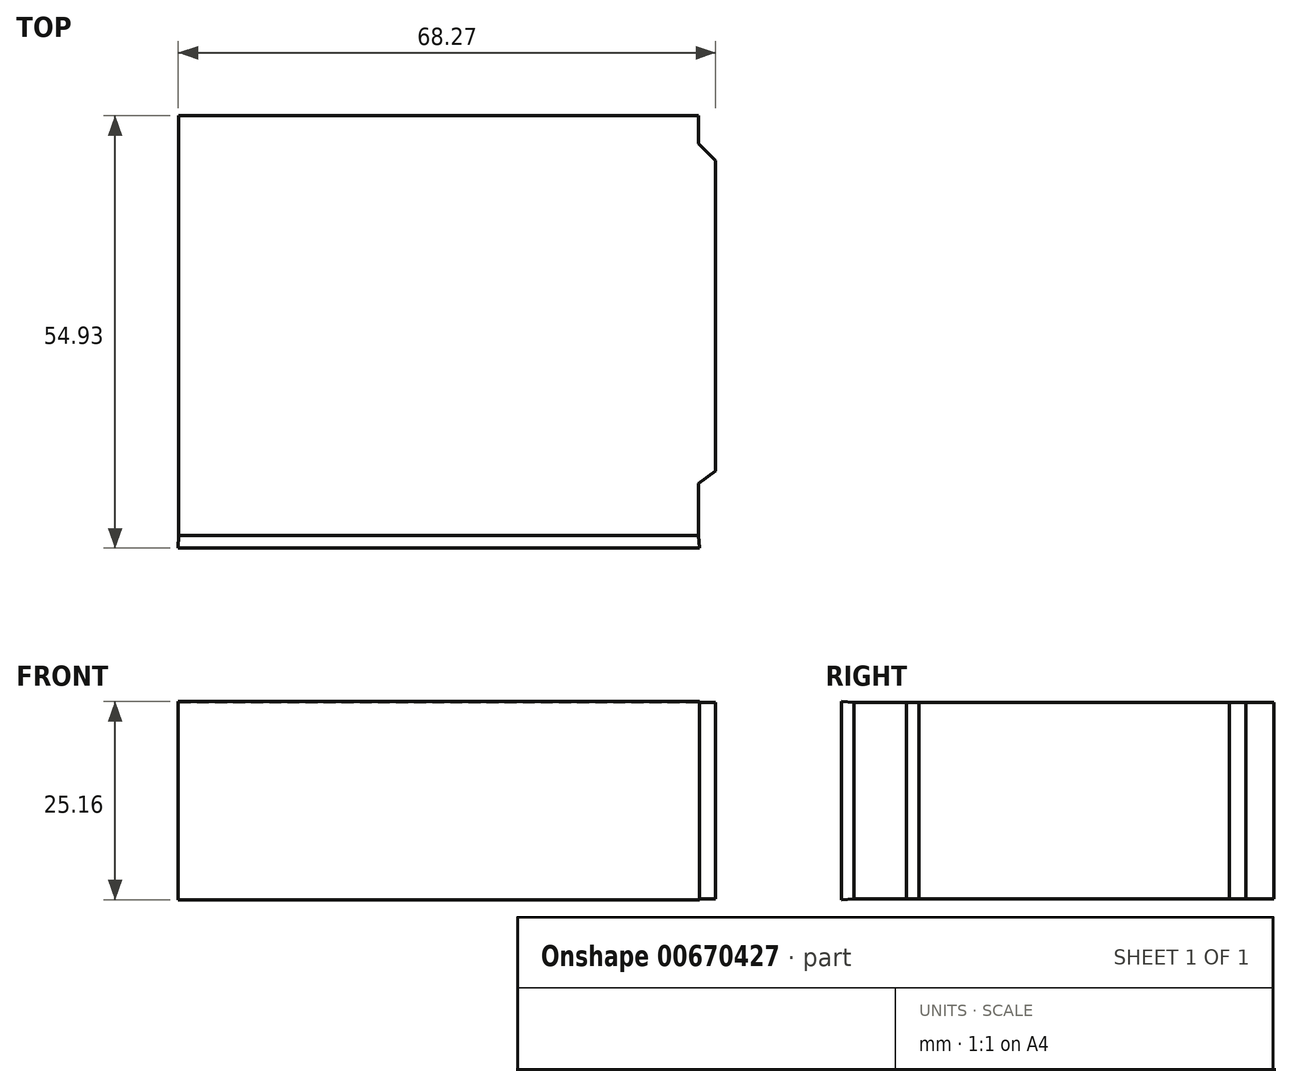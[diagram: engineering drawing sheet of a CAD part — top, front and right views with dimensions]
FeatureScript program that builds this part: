
annotation { "Feature Type Name" : "Feature", "Feature Type Description" : "" }
export const myFeature = defineFeature(function(context is Context, id is Id, definition is map)
    precondition{}
    {
        {
            var Q0;
            Q0=qCreatedBy(makeId("Top.planeOp"),FACE);
            var sketch = newSketch(context, id + "F0", { "sketchPlane" : qUnion([Q0])});
            skLineSegment(sketch, "E0", {"start": v(-33.63, 23.99) * mm, "end": v(32.41, 23.99) * mm});
            skLineSegment(sketch, "E1", {"start": v(32.41, 23.99) * mm, "end": v(32.41, 20.43) * mm});
            skLineSegment(sketch, "E2", {"start": v(-33.63, -29.35) * mm, "end": v(-33.63, 23.99) * mm});
            skLineSegment(sketch, "E3", {"start": v(34.56, 18.29) * mm, "end": v(34.56, -21.13) * mm});
            skLineSegment(sketch, "E4", {"start": v(34.56, -21.13) * mm, "end": v(32.41, -22.7) * mm});
            skLineSegment(sketch, "E5", {"start": v(32.41, 20.43) * mm, "end": v(34.56, 18.29) * mm});
            skLineSegment(sketch, "E6", {"start": v(-0.6, -2.68) * mm, "end": v(-33.63, -2.68) * mm, "construction": true});
            skLineSegment(sketch, "E7", {"start": v(-33.63, -29.35) * mm, "end": v(32.41, -29.35) * mm});
            skLineSegment(sketch, "E8", {"start": v(-0.6, -29.35) * mm, "end": v(-0.6, -2.68) * mm, "construction": true});
            skLineSegment(sketch, "E9.trimOffspring", {"start": v(32.41, -22.7) * mm, "end": v(32.41, -29.35) * mm});
            skSolve(sketch);
        }
        {
            var Q0;
            Q0=makeQuery(id+"F0.imprint","IMPRINT",FACE,{"disambiguationData":[TD([[makeQuery(id+"F0.imprint","IMPRINT",EDGE,{"derivedFrom":sQuery(id+"F0.wireOp",EDGE,"E0")}),-1.0]])]});
            extrude(context, id + "F1", {"entities" : qUnion([Q0]), "depth" : 25 * mm, "offsetDistance" : 25 * mm});
        }
        {
            var Q0;
            Q0=makeQuery(id+"F1.opExtrude","SWEPT_FACE",FACE,{"disambiguationData":[OSD([sQuery(id+"F0.wireOp",EDGE,"E7")])]});
            extrude(context, id + "F2", {"entities" : qUnion([Q0]), "operationType" : NewBodyOperationType.ADD, "depth" : 1.59 * mm, "offsetDistance" : 25 * mm, "hasDraft" : true, "draftAngle" : 3 * degree});
        }
    });
